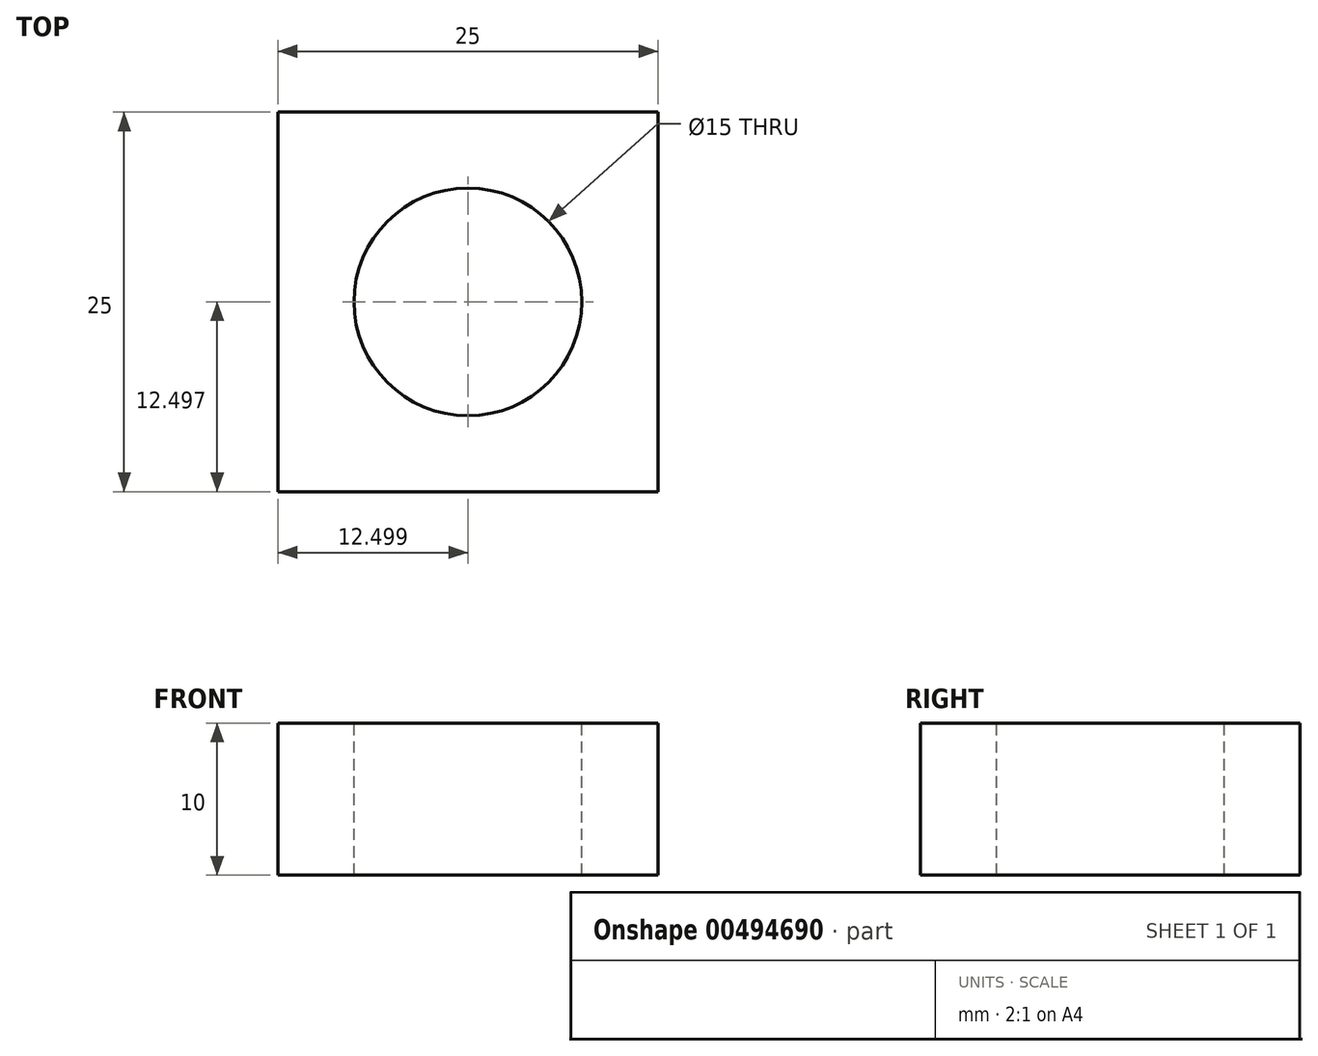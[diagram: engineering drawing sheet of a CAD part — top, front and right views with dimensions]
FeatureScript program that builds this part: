
annotation { "Feature Type Name" : "Feature", "Feature Type Description" : "" }
export const myFeature = defineFeature(function(context is Context, id is Id, definition is map)
    precondition{}
    {
        {
            var Q0;
            Q0=qCreatedBy(makeId("Top.planeOp"),FACE);
            var sketch = newSketch(context, id + "F0", { "sketchPlane" : qUnion([Q0])});
            skLineSegment(sketch, "E0.bottom", {"start": v(-61.98, -61.88) * mm, "end": v(-36.98, -61.88) * mm});
            skLineSegment(sketch, "E0.top", {"start": v(-61.98, -36.88) * mm, "end": v(-36.98, -36.88) * mm});
            skLineSegment(sketch, "E0.left", {"start": v(-61.98, -61.88) * mm, "end": v(-61.98, -36.88) * mm});
            skLineSegment(sketch, "E0.right", {"start": v(-36.98, -61.88) * mm, "end": v(-36.98, -36.88) * mm});
            skSolve(sketch);
        }
        {
            var Q0;
            Q0=qSketchRegion(id+"F0",true);
            extrude(context, id + "F1", {"entities" : qUnion([Q0]), "depth" : 10 * mm});
        }
        {
            var Q0;
            Q0=makeQuery(id+"F1.opExtrude","CAP_FACE",FACE,{"disambiguationData":[OSD([sQuery(id+"F0.wireOp",EDGE,"E0.bottom"),sQuery(id+"F0.wireOp",EDGE,"E0.top"),sQuery(id+"F0.wireOp",EDGE,"E0.left"),sQuery(id+"F0.wireOp",EDGE,"E0.right")])],"isStart":false});
            var sketch = newSketch(context, id + "F2", { "sketchPlane" : qUnion([Q0])});
            skLineSegment(sketch, "E1", {"start": v(-61.98, -61.88) * mm, "end": v(-49.48, -61.88) * mm});
            skLineSegment(sketch, "E2", {"start": v(-36.98, -61.88) * mm, "end": v(-36.98, -49.38) * mm});
            skCircle(sketch, "E3", {"center": v(-49.48, -49.38) * mm, "radius": 7.5 * mm});
            skSolve(sketch);
        }
        {
            var Q0;
            Q0=makeQuery(id+"F2.imprint","IMPRINT",FACE,{"disambiguationData":[TD([[makeQuery(id+"F2.imprint","IMPRINT",EDGE,{"derivedFrom":sQuery(id+"F2.wireOp",EDGE,"E3")}),1.0]])]});
            extrude(context, id + "F3", {"entities" : qUnion([Q0]), "operationType" : NewBodyOperationType.REMOVE, "oppositeDirection" : true, "depth" : 10 * mm});
        }
    });
